# Revit family: FU_Inspec_Campus_3-1
name_source: partatom
category: Furniture
units: mm (PartAtom-declared; Revit-internal decimal feet)

## family parameters
Always vertical = Yes
Cut with Voids When Loaded = No
OmniClass Number = 23.40.20.00
OmniClass Title = General Furniture and Specialties
Room Calculation Point = No
Shared = No
Work Plane-Based = No

## types (3) — shared parameters
Assembly Code = E2020
Description = *Please enter mtrl description here for use in mto*
Keynote = 46.B
Manufacturer = LAMMHULTS
Model = CAMPUS
URL = www.lammhults.se
zero-valued in all types: Default Elevation

## per-type parameters (varying)
| type | Back Material | Frame Material | Seat Material |
| Campus 3.1 - Chrome - Oak | Wood - Veneer - Oak | Metal - Chrome - Polished | Wood - Veneer - Oak |
| Campus 3.2 - White - Oak - Red | Wood - Veneer - Oak | Metal - White - Matte | Fabric - Red |
| Campus 3.3 - Graphite - Red | Fabric - Red | Metal - Graphite - Matte | Fabric - Red |

## geometry (parser evidence)
native form markers: Blend x8, Sweep x2
no freeform markers — native parametric forms only
